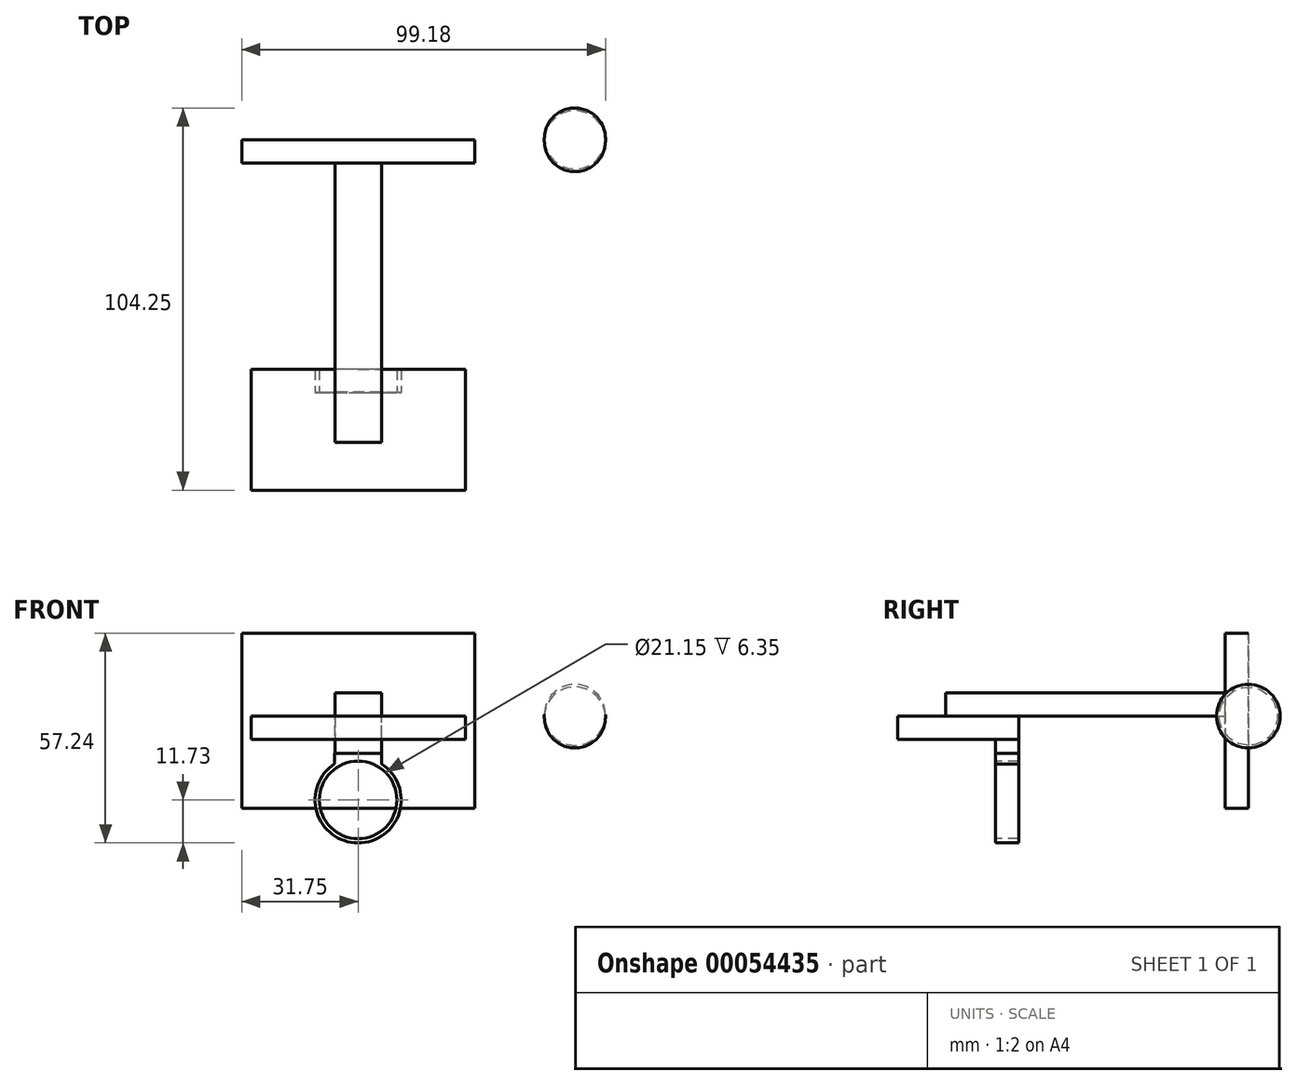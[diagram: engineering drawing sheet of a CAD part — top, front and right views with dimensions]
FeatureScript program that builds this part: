
annotation { "Feature Type Name" : "Feature", "Feature Type Description" : "" }
export const myFeature = defineFeature(function(context is Context, id is Id, definition is map)
    precondition{}
    {
        {
            var Q0;
            Q0=qCreatedBy(makeId("Front.planeOp"),FACE);
            var sketch = newSketch(context, id + "F0", { "sketchPlane" : qUnion([Q0])});
            skLineSegment(sketch, "E0", {"start": v(0, 31.75) * mm, "end": v(31.75, 31.75) * mm});
            skLineSegment(sketch, "E1", {"start": v(31.75, 31.75) * mm, "end": v(31.75, 0) * mm});
            skLineSegment(sketch, "E2", {"start": v(31.75, 0) * mm, "end": v(31.75, -31.75) * mm});
            skLineSegment(sketch, "E3", {"start": v(31.75, -31.75) * mm, "end": v(0, -31.75) * mm});
            skLineSegment(sketch, "E4", {"start": v(0, -31.75) * mm, "end": v(-31.75, -31.75) * mm});
            skLineSegment(sketch, "E5", {"start": v(-31.75, -31.75) * mm, "end": v(-31.75, 0) * mm});
            skLineSegment(sketch, "E6", {"start": v(-31.75, 0) * mm, "end": v(-31.75, 31.75) * mm});
            skLineSegment(sketch, "E7", {"start": v(-31.75, 31.75) * mm, "end": v(0, 31.75) * mm});
            skSolve(sketch);
        }
        {
            var Q0;
            Q0=makeQuery(id+"F0.imprint","IMPRINT",FACE,{"disambiguationData":[TD([[makeQuery(id+"F0.imprint","IMPRINT",EDGE,{"derivedFrom":sQuery(id+"F0.wireOp",EDGE,"E0")}),-1.0]])]});
            extrude(context, id + "F1", {"entities" : qUnion([Q0]), "depth" : 6.35 * mm});
        }
        {
            var Q0;
            Q0=makeQuery(id+"F1.opExtrude","CAP_FACE",FACE,{"disambiguationData":[OSD([sQuery(id+"F0.wireOp",EDGE,"E0"),sQuery(id+"F0.wireOp",EDGE,"E1"),sQuery(id+"F0.wireOp",EDGE,"E2"),sQuery(id+"F0.wireOp",EDGE,"E3"),sQuery(id+"F0.wireOp",EDGE,"E4"),sQuery(id+"F0.wireOp",EDGE,"E5"),sQuery(id+"F0.wireOp",EDGE,"E6"),sQuery(id+"F0.wireOp",EDGE,"E7")])],"isStart":false});
            var sketch = newSketch(context, id + "F2", { "sketchPlane" : qUnion([Q0])});
            skLineSegment(sketch, "E8", {"start": v(-6.35, 0) * mm, "end": v(-6.35, 6.35) * mm});
            skLineSegment(sketch, "E9", {"start": v(-6.35, 6.35) * mm, "end": v(6.35, 6.35) * mm});
            skLineSegment(sketch, "E10", {"start": v(6.35, 6.35) * mm, "end": v(6.35, 0) * mm});
            skLineSegment(sketch, "E11", {"start": v(6.35, 0) * mm, "end": v(0, 0) * mm});
            skLineSegment(sketch, "E12", {"start": v(0, 0) * mm, "end": v(-6.35, 0) * mm});
            skSolve(sketch);
        }
        {
            var Q0;
            Q0=makeQuery(id+"F2.imprint","IMPRINT",FACE,{"disambiguationData":[TD([[makeQuery(id+"F2.imprint","IMPRINT",EDGE,{"derivedFrom":sQuery(id+"F2.wireOp",EDGE,"E8")}),-1.0]])]});
            extrude(context, id + "F3", {"entities" : qUnion([Q0]), "operationType" : NewBodyOperationType.ADD, "depth" : 76.2 * mm});
        }
        {
            var Q0;
            Q0=qCreatedBy(makeId("Top.planeOp"),FACE);
            var sketch = newSketch(context, id + "F4", { "sketchPlane" : qUnion([Q0])});
            skLineSegment(sketch, "E13", {"start": v(0, -95.57) * mm, "end": v(29.21, -95.57) * mm});
            skLineSegment(sketch, "E14", {"start": v(29.21, -95.57) * mm, "end": v(29.21, -62.55) * mm});
            skLineSegment(sketch, "E15", {"start": v(29.21, -62.55) * mm, "end": v(-29.21, -62.55) * mm});
            skLineSegment(sketch, "E16", {"start": v(-29.21, -62.55) * mm, "end": v(-29.21, -95.57) * mm});
            skLineSegment(sketch, "E17", {"start": v(-29.21, -95.57) * mm, "end": v(0, -95.57) * mm});
            skSolve(sketch);
        }
        {
            var Q0;
            Q0=makeQuery(id+"F4.imprint","IMPRINT",FACE,{"disambiguationData":[TD([[makeQuery(id+"F4.imprint","IMPRINT",EDGE,{"derivedFrom":sQuery(id+"F4.wireOp",EDGE,"E13")}),1.0]])]});
            extrude(context, id + "F5", {"entities" : qUnion([Q0]), "operationType" : NewBodyOperationType.ADD, "oppositeDirection" : true, "depth" : 6.35 * mm});
        }
        {
            var Q0;
            Q0=qCreatedBy(makeId("Top.planeOp"),FACE);
            var sketch = newSketch(context, id + "F6", { "sketchPlane" : qUnion([Q0])});
            skLineSegment(sketch, "E18", {"start": v(6.35, -62.54) * mm, "end": v(6.35, -68.89) * mm});
            skLineSegment(sketch, "E19", {"start": v(6.35, -68.89) * mm, "end": v(-6.35, -68.89) * mm});
            skLineSegment(sketch, "E20", {"start": v(-6.35, -68.89) * mm, "end": v(-6.35, -62.54) * mm});
            skLineSegment(sketch, "E21", {"start": v(-6.35, -62.54) * mm, "end": v(0, -62.54) * mm});
            skLineSegment(sketch, "E22", {"start": v(0, -62.54) * mm, "end": v(6.35, -62.54) * mm});
            skSolve(sketch);
        }
        {
            var Q0;
            Q0 = qSketchRegion(id + "F6", true);
            extrude(context, id + "F7", {"entities" : qUnion([Q0]), "operationType" : NewBodyOperationType.ADD, "oppositeDirection" : true, "depth" : 10.16 * mm});
        }
        {
            var Q0;
            Q0=makeQuery(id+"F7.opExtrude","CAP_FACE",FACE,{"disambiguationData":[OSD([sQuery(id+"F6.wireOp",EDGE,"E18"),sQuery(id+"F6.wireOp",EDGE,"E19"),sQuery(id+"F6.wireOp",EDGE,"E20"),sQuery(id+"F6.wireOp",EDGE,"E21"),sQuery(id+"F6.wireOp",EDGE,"E22")])],"isStart":false});
            var sketch = newSketch(context, id + "F8", { "sketchPlane" : qUnion([Q0])});
            skLineSegment(sketch, "E23", {"start": v(-12.7, 68.91) * mm, "end": v(12.7, 68.91) * mm});
            skLineSegment(sketch, "E24", {"start": v(12.7, 68.91) * mm, "end": v(12.7, 62.56) * mm});
            skLineSegment(sketch, "E25", {"start": v(12.7, 62.56) * mm, "end": v(-12.7, 62.56) * mm});
            skLineSegment(sketch, "E26", {"start": v(-12.7, 62.56) * mm, "end": v(-12.7, 68.91) * mm});
            skSolve(sketch);
        }
        {
            var Q0;
            {var subQ5=makeQuery(id+"F7.opExtrude","CAP_EDGE",EDGE,{"disambiguationData":[OSD([sQuery(id+"F6.wireOp",EDGE,"E19")])],"isStart":false});Q0=makeQuery(id+"F8.imprint","IMPRINT",FACE,{"disambiguationData":[TD([[makeQuery(id+"F8.imprint","IMPRINT",EDGE,{"derivedFrom":subQ5}),1.0]])]});}
            var Q1;
            Q1=makeQuery(id+"F8.imprint","IMPRINT",FACE,{"disambiguationData":[TD([[makeQuery(id+"F8.imprint","IMPRINT",EDGE,{"derivedFrom":sQuery(id+"F8.wireOp",EDGE,"E23")}),-1.0]])]});
            extrude(context, id + "F9", {"entities" : qUnion([Q0, Q1]), "operationType" : NewBodyOperationType.ADD, "depth" : 25.4 * mm});
        }
        {
            var Q0;
            Q0=makeQuery(id+"F9.opExtrude","SWEPT_FACE",FACE,{"disambiguationData":[OSD([sQuery(id+"F8.wireOp",EDGE,"E23")])]});
            var sketch = newSketch(context, id + "F10", { "sketchPlane" : qUnion([Q0])});
            skCircle(sketch, "E27", {"center": v(0, -22.86) * mm, "radius": 11.73 * mm});
            skCircle(sketch, "E28", {"center": v(0, -22.86) * mm, "radius": 10.57 * mm});
            skLineSegment(sketch, "E29", {"start": v(-6.37, -10.16) * mm, "end": v(-6.37, -13.01) * mm});
            skLineSegment(sketch, "E30", {"start": v(6.43, -10.16) * mm, "end": v(6.43, -13.05) * mm});
            skSolve(sketch);
        }
        {
            var Q0;
            {var subQ3=sQuery(id+"F10.wireOp",EDGE,"E29");Q0=makeQuery(id+"F10.imprint","IMPRINT",FACE,{"disambiguationData":[TD([[makeQuery(id+"F10.imprint","IMPRINT",EDGE,{"derivedFrom":subQ3}),-1.0]])]});}
            var Q1;
            Q1=makeQuery(id+"F10.imprint","IMPRINT",FACE,{"disambiguationData":[TD([[makeQuery(id+"F10.imprint","IMPRINT",EDGE,{"derivedFrom":sQuery(id+"F10.wireOp",EDGE,"E28")}),1.0]])]});
            extrude(context, id + "F11", {"entities" : qUnion([Q0, Q1]), "operationType" : NewBodyOperationType.REMOVE, "oppositeDirection" : true, "depth" : 25.4 * mm});
        }
        {
            var Q0;
            Q0=makeQuery(id+"F1.opExtrude","CAP_FACE",FACE,{"disambiguationData":[OSD([sQuery(id+"F0.wireOp",EDGE,"E0"),sQuery(id+"F0.wireOp",EDGE,"E1"),sQuery(id+"F0.wireOp",EDGE,"E2"),sQuery(id+"F0.wireOp",EDGE,"E3"),sQuery(id+"F0.wireOp",EDGE,"E4"),sQuery(id+"F0.wireOp",EDGE,"E5"),sQuery(id+"F0.wireOp",EDGE,"E6"),sQuery(id+"F0.wireOp",EDGE,"E7")])],"isStart":false});
            var sketch = newSketch(context, id + "F12", { "sketchPlane" : qUnion([Q0])});
            skLineSegment(sketch, "E31", {"start": v(-31.75, 22.65) * mm, "end": v(31.75, 22.65) * mm});
            skLineSegment(sketch, "E32", {"start": v(-31.75, -25.11) * mm, "end": v(31.75, -25.11) * mm});
            skSolve(sketch);
        }
        {
            var Q0;
            {var subQ0=sQuery(id+"F12.wireOp",EDGE,"E31");Q0=makeQuery(id+"F12.imprint","IMPRINT",FACE,{"disambiguationData":[TD([[makeQuery(id+"F12.imprint","IMPRINT",EDGE,{"derivedFrom":subQ0}),1.0]])]});}
            var Q1;
            {var subQ0=sQuery(id+"F12.wireOp",EDGE,"E32");Q1=makeQuery(id+"F12.imprint","IMPRINT",FACE,{"disambiguationData":[TD([[makeQuery(id+"F12.imprint","IMPRINT",EDGE,{"derivedFrom":subQ0}),-1.0]])]});}
            extrude(context, id + "F13", {"entities" : qUnion([Q0, Q1]), "operationType" : NewBodyOperationType.REMOVE, "oppositeDirection" : true, "depth" : 25.4 * mm});
        }
        {
            var Q0;
            Q0=qCreatedBy(makeId("Top.planeOp"),FACE);
            var sketch = newSketch(context, id + "F14", { "sketchPlane" : qUnion([Q0])});
            skArc(sketch, "E33", {"start": v(50.78, 0) * mm, "mid": v(59.1, -8.68) * mm, "end": v(67.43, 0) * mm});
            skLineSegment(sketch, "E34", {"start": v(50.78, 0) * mm, "end": v(67.43, 0) * mm});
            skSolve(sketch);
        }
        {
            var Q0;
            Q0=makeQuery(id+"F14.imprint","IMPRINT",FACE,{"disambiguationData":[TD([[makeQuery(id+"F14.imprint","IMPRINT",EDGE,{"derivedFrom":sQuery(id+"F14.wireOp",EDGE,"E33")}),1.0]])]});
            var Q1;
            Q1=sQuery(id+"F14.wireOp",EDGE,"E34");
            revolve(context, id + "F15", {"entities" : qUnion([Q0]), "axis" : qUnion([Q1]), "revolveType" : RevolveType.FULL});
        }
    });
